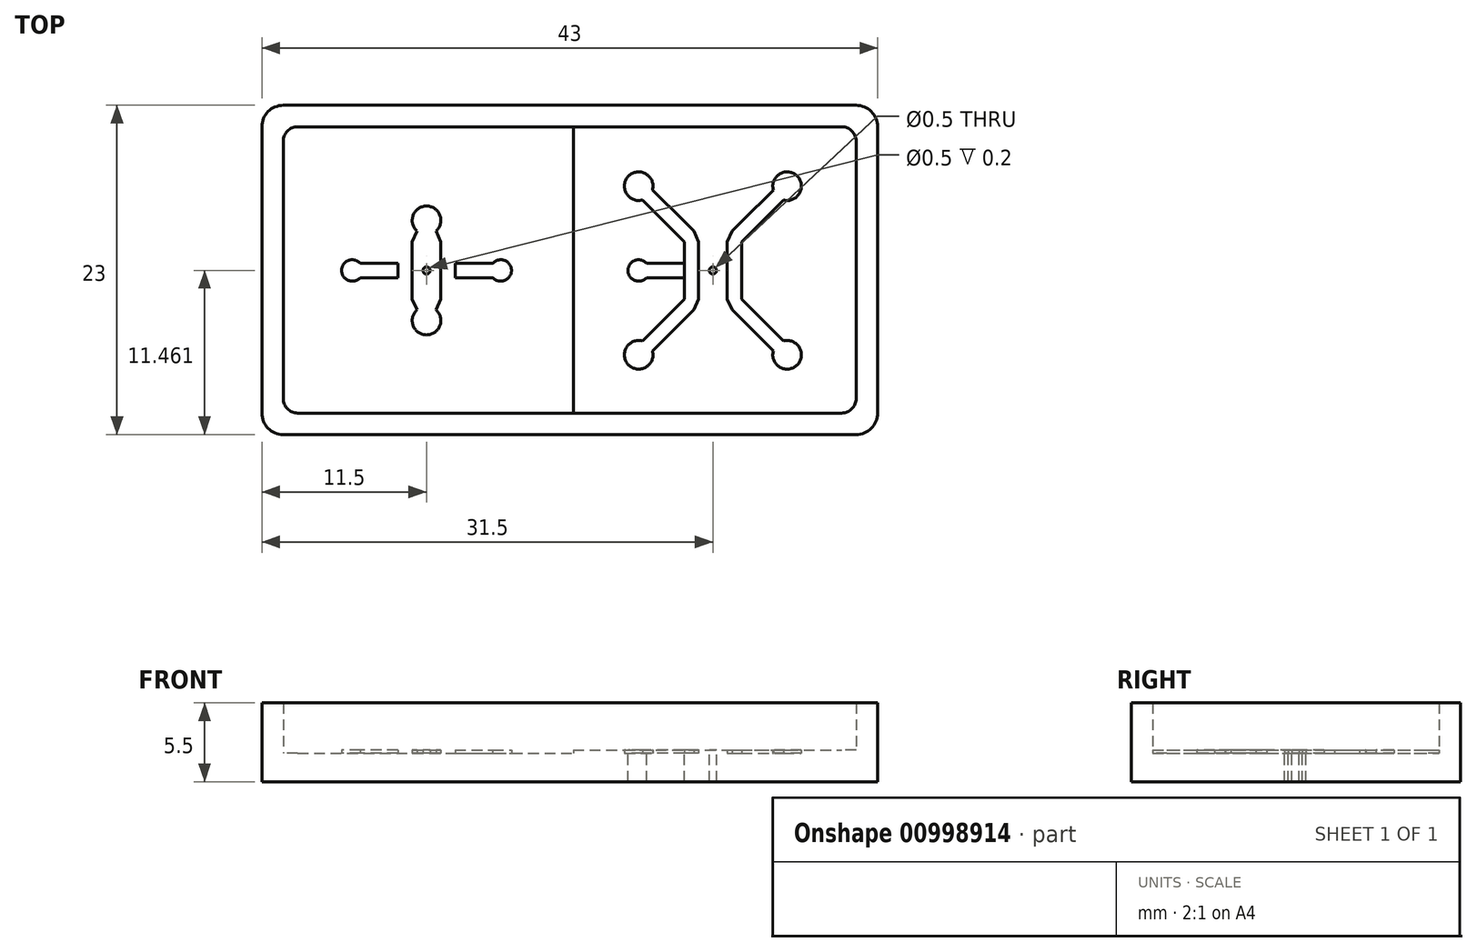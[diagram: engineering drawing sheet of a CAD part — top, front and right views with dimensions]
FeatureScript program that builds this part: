
annotation { "Feature Type Name" : "Feature", "Feature Type Description" : "" }
export const myFeature = defineFeature(function(context is Context, id is Id, definition is map)
    precondition{}
    {
        {
            var Q0;
            Q0=qCreatedBy(makeId("Top.planeOp"),FACE);
            var sketch = newSketch(context, id + "F0", { "sketchPlane" : qUnion([Q0])});
            skLineSegment(sketch, "E0.bottom", {"start": v(1, 0) * mm, "end": v(39, 0) * mm});
            skLineSegment(sketch, "E0.top", {"start": v(1, 20) * mm, "end": v(39, 20) * mm});
            skLineSegment(sketch, "E0.left", {"start": v(0, 1) * mm, "end": v(0, 19) * mm});
            skLineSegment(sketch, "E0.right", {"start": v(40, 1) * mm, "end": v(40, 19) * mm});
            skLineSegment(sketch, "E1.right", {"start": v(11, 9.96) * mm, "end": v(11, 11.96) * mm});
            skLineSegment(sketch, "E2.MirrorCS", {"start": v(9, 9.96) * mm, "end": v(9, 11.96) * mm});
            skLineSegment(sketch, "E3.MirrorCS", {"start": v(11, 9.96) * mm, "end": v(11, 7.96) * mm});
            skLineSegment(sketch, "E4.MirrorCS", {"start": v(9, 9.96) * mm, "end": v(9, 7.96) * mm});
            skLineSegment(sketch, "E5", {"start": v(10.66, 7.21) * mm, "end": v(11, 7.96) * mm});
            skLineSegment(sketch, "E6", {"start": v(9, 7.96) * mm, "end": v(9.34, 7.21) * mm});
            skCircle(sketch, "E7", {"center": v(10, 9.96) * mm, "radius": 0.25 * mm});
            skArc(sketch, "E8", {"start": v(9.34, 7.21) * mm, "mid": v(10, 5.46) * mm, "end": v(10.66, 7.21) * mm});
            skLineSegment(sketch, "E9.left", {"start": v(11, 11.96) * mm, "end": v(11, 9.96) * mm});
            skLineSegment(sketch, "E9.right", {"start": v(12, 11.96) * mm, "end": v(12, 9.96) * mm});
            skLineSegment(sketch, "E10.MirrorCS", {"start": v(12, 7.96) * mm, "end": v(12, 9.96) * mm});
            skLineSegment(sketch, "E11", {"start": v(11, 7.96) * mm, "end": v(11.34, 7.21) * mm});
            skLineSegment(sketch, "E12", {"start": v(11.34, 7.21) * mm, "end": v(12, 6.55) * mm});
            skLineSegment(sketch, "E13", {"start": v(12, 6.55) * mm, "end": v(14.22, 4.33) * mm});
            skArc(sketch, "E14", {"start": v(14.22, 4.33) * mm, "mid": v(15.89, 3.36) * mm, "end": v(14.92, 5.04) * mm});
            skArc(sketch, "E15.MirrorCS", {"start": v(9.34, 12.71) * mm, "mid": v(10, 14.46) * mm, "end": v(10.66, 12.71) * mm});
            skLineSegment(sketch, "E16.MirrorCS", {"start": v(10.66, 12.71) * mm, "end": v(11, 11.96) * mm});
            skLineSegment(sketch, "E17.MirrorCS", {"start": v(9, 11.96) * mm, "end": v(9.34, 12.71) * mm});
            skLineSegment(sketch, "E18.MirrorCS", {"start": v(11, 11.96) * mm, "end": v(11.34, 12.71) * mm});
            skLineSegment(sketch, "E19.MirrorCS", {"start": v(11.34, 12.71) * mm, "end": v(12, 13.37) * mm});
            skLineSegment(sketch, "E20.MirrorCS", {"start": v(12, 13.37) * mm, "end": v(14.22, 15.6) * mm});
            skArc(sketch, "E21.MirrorCS", {"start": v(14.22, 15.6) * mm, "mid": v(15.89, 16.56) * mm, "end": v(14.92, 14.88) * mm});
            skLineSegment(sketch, "E22", {"start": v(12, 7.96) * mm, "end": v(14.92, 5.04) * mm});
            skLineSegment(sketch, "E23.MirrorCS", {"start": v(12, 11.96) * mm, "end": v(14.92, 14.88) * mm});
            skLineSegment(sketch, "E24.MirrorCS", {"start": v(9, 11.96) * mm, "end": v(8.66, 12.71) * mm});
            skLineSegment(sketch, "E25.MirrorCS", {"start": v(9, 7.96) * mm, "end": v(8.66, 7.21) * mm});
            skLineSegment(sketch, "E26.MirrorCS", {"start": v(8.66, 12.71) * mm, "end": v(8, 13.37) * mm});
            skLineSegment(sketch, "E27.MirrorCS", {"start": v(8, 13.37) * mm, "end": v(5.78, 15.6) * mm});
            skArc(sketch, "E28.MirrorCS", {"start": v(5.78, 15.6) * mm, "mid": v(4.11, 16.56) * mm, "end": v(5.08, 14.88) * mm});
            skLineSegment(sketch, "E29.MirrorCS", {"start": v(8, 11.96) * mm, "end": v(5.08, 14.88) * mm});
            skLineSegment(sketch, "E30.MirrorCS", {"start": v(8, 11.96) * mm, "end": v(8, 9.96) * mm});
            skLineSegment(sketch, "E31.MirrorCS", {"start": v(8, 7.96) * mm, "end": v(8, 9.96) * mm});
            skArc(sketch, "E32.MirrorCS", {"start": v(5.78, 4.33) * mm, "mid": v(4.11, 3.36) * mm, "end": v(5.08, 5.04) * mm});
            skLineSegment(sketch, "E33.MirrorCS", {"start": v(8, 7.96) * mm, "end": v(5.08, 5.04) * mm});
            skLineSegment(sketch, "E34.MirrorCS", {"start": v(8, 6.55) * mm, "end": v(5.78, 4.33) * mm});
            skLineSegment(sketch, "E35.MirrorCS", {"start": v(8.66, 7.21) * mm, "end": v(8, 6.55) * mm});
            skLineSegment(sketch, "E36", {"start": v(12, 10.46) * mm, "end": v(14.62, 10.46) * mm});
            skLineSegment(sketch, "E37", {"start": v(12, 9.46) * mm, "end": v(14.62, 9.46) * mm});
            skArc(sketch, "E38", {"start": v(14.81, 10.61) * mm, "mid": v(14.71, 10.55) * mm, "end": v(14.62, 10.46) * mm});
            skArc(sketch, "E39", {"start": v(14.62, 9.46) * mm, "mid": v(15.92, 9.84) * mm, "end": v(14.81, 10.61) * mm});
            skLineSegment(sketch, "E40.MirrorCS", {"start": v(8, 10.46) * mm, "end": v(5.38, 10.46) * mm});
            skLineSegment(sketch, "E41.MirrorCS", {"start": v(8, 9.46) * mm, "end": v(5.38, 9.46) * mm});
            skArc(sketch, "E42.MirrorCS", {"start": v(5.38, 9.46) * mm, "mid": v(4.08, 9.84) * mm, "end": v(5.19, 10.61) * mm});
            skArc(sketch, "E43.MirrorCS", {"start": v(5.19, 10.61) * mm, "mid": v(5.29, 10.55) * mm, "end": v(5.38, 10.46) * mm});
            skPoint(sketch, "E44.startSnap0", {"position": v(16, 9.96) * mm});
            skPoint(sketch, "E44.startSnap1", {"position": v(15.92, 9.84) * mm});
            skPoint(sketch, "E44.endSnap0", {"position": v(15.92, 9.84) * mm});
            skLineSegment(sketch, "E45", {"start": v(-1.5, 20) * mm, "end": v(-1.5, 0) * mm});
            skLineSegment(sketch, "E46", {"start": v(0, 21.5) * mm, "end": v(40, 21.5) * mm});
            skArc(sketch, "E47", {"start": v(0, 21.5) * mm, "mid": v(-1.06, 21.06) * mm, "end": v(-1.5, 20) * mm});
            skLineSegment(sketch, "E48.MirrorCS", {"start": v(0, -1.5) * mm, "end": v(40, -1.5) * mm});
            skArc(sketch, "E49.MirrorCS", {"start": v(0, -1.5) * mm, "mid": v(-1.06, -1.06) * mm, "end": v(-1.5, 0) * mm});
            skArc(sketch, "E50.MirrorCS", {"start": v(40, 21.5) * mm, "mid": v(41.06, 21.06) * mm, "end": v(41.5, 20) * mm});
            skLineSegment(sketch, "E51.MirrorCS", {"start": v(41.5, 20) * mm, "end": v(41.5, 0) * mm});
            skArc(sketch, "E52.MirrorCS", {"start": v(40, -1.5) * mm, "mid": v(41.06, -1.06) * mm, "end": v(41.5, 0) * mm});
            skArc(sketch, "E53.filletArc", {"start": v(1, 20) * mm, "mid": v(0.3, 19.7) * mm, "end": v(0, 19) * mm});
            skArc(sketch, "E54.filletArc", {"start": v(40, 19) * mm, "mid": v(39.7, 19.7) * mm, "end": v(39, 20) * mm});
            skArc(sketch, "E55.filletArc", {"start": v(39, 0) * mm, "mid": v(39.7, 0.3) * mm, "end": v(40, 1) * mm});
            skArc(sketch, "E56.filletArc", {"start": v(0, 1) * mm, "mid": v(0.3, 0.3) * mm, "end": v(1, 0) * mm});
            skLineSegment(sketch, "E57.MirrorCS", {"start": v(31.34, 12.71) * mm, "end": v(32, 13.37) * mm});
            skLineSegment(sketch, "E58.MirrorCS", {"start": v(29, 11.96) * mm, "end": v(28.66, 12.71) * mm});
            skLineSegment(sketch, "E59.MirrorCS", {"start": v(31.34, 7.21) * mm, "end": v(32, 6.55) * mm});
            skLineSegment(sketch, "E60.MirrorCS", {"start": v(28.66, 7.21) * mm, "end": v(28, 6.55) * mm});
            skLineSegment(sketch, "E61.MirrorCS", {"start": v(31, 11.96) * mm, "end": v(31.34, 12.71) * mm});
            skLineSegment(sketch, "E62.MirrorCS", {"start": v(29.34, 7.21) * mm, "end": v(29, 7.96) * mm});
            skArc(sketch, "E63.MirrorCS", {"start": v(25.19, 10.61) * mm, "mid": v(25.29, 10.55) * mm, "end": v(25.38, 10.46) * mm});
            skLineSegment(sketch, "E64.MirrorCS", {"start": v(31, 11.96) * mm, "end": v(30.66, 12.71) * mm});
            skArc(sketch, "E65.MirrorCS", {"start": v(34.81, 10.61) * mm, "mid": v(34.71, 10.55) * mm, "end": v(34.62, 10.46) * mm});
            skLineSegment(sketch, "E66.MirrorCS", {"start": v(29.34, 12.71) * mm, "end": v(29, 11.96) * mm});
            skLineSegment(sketch, "E67.MirrorCS", {"start": v(29, 7.96) * mm, "end": v(28.66, 7.21) * mm});
            skLineSegment(sketch, "E68.MirrorCS", {"start": v(28.66, 12.71) * mm, "end": v(28, 13.37) * mm});
            skLineSegment(sketch, "E69.MirrorCS", {"start": v(31, 7.96) * mm, "end": v(30.66, 7.21) * mm});
            skLineSegment(sketch, "E70.MirrorCS", {"start": v(29, 9.96) * mm, "end": v(29, 11.96) * mm});
            skCircle(sketch, "E71.MirrorC", {"center": v(30, 9.96) * mm, "radius": 0.25 * mm});
            skLineSegment(sketch, "E72.MirrorCS", {"start": v(31, 7.96) * mm, "end": v(31.34, 7.21) * mm});
            skPoint(sketch, "E73.MirrorP", {"position": v(24.08, 9.84) * mm});
            skLineSegment(sketch, "E74.MirrorCS", {"start": v(31, 9.96) * mm, "end": v(31, 11.96) * mm});
            skLineSegment(sketch, "E75.MirrorCS", {"start": v(28, 11.96) * mm, "end": v(28, 9.96) * mm});
            skPoint(sketch, "E76.MirrorP", {"position": v(24, 9.96) * mm});
            skLineSegment(sketch, "E77.MirrorCS", {"start": v(29, 11.96) * mm, "end": v(29, 9.96) * mm});
            skLineSegment(sketch, "E78.MirrorCS", {"start": v(29, 9.96) * mm, "end": v(29, 7.96) * mm});
            skArc(sketch, "E79.MirrorCS", {"start": v(34.22, 15.6) * mm, "mid": v(35.89, 16.56) * mm, "end": v(34.92, 14.88) * mm});
            skLineSegment(sketch, "E80.MirrorCS", {"start": v(32, 11.96) * mm, "end": v(34.92, 14.88) * mm});
            skLineSegment(sketch, "E81.MirrorCS", {"start": v(28, 11.96) * mm, "end": v(25.08, 14.88) * mm});
            skLineSegment(sketch, "E82.MirrorCS", {"start": v(28, 7.96) * mm, "end": v(25.08, 5.04) * mm});
            skArc(sketch, "E83.MirrorCS", {"start": v(30.66, 7.21) * mm, "mid": v(30, 5.46) * mm, "end": v(29.34, 7.21) * mm});
            skArc(sketch, "E84.MirrorCS", {"start": v(25.78, 4.33) * mm, "mid": v(24.11, 3.36) * mm, "end": v(25.08, 5.04) * mm});
            skLineSegment(sketch, "E85.MirrorCS", {"start": v(31, 9.96) * mm, "end": v(31, 7.96) * mm});
            skLineSegment(sketch, "E86.MirrorCS", {"start": v(32, 6.55) * mm, "end": v(34.22, 4.33) * mm});
            skLineSegment(sketch, "E87.MirrorCS", {"start": v(32, 10.46) * mm, "end": v(34.62, 10.46) * mm});
            skArc(sketch, "E88.MirrorCS", {"start": v(25.78, 15.6) * mm, "mid": v(24.11, 16.56) * mm, "end": v(25.08, 14.88) * mm});
            skLineSegment(sketch, "E89.MirrorCS", {"start": v(32, 13.37) * mm, "end": v(34.22, 15.6) * mm});
            skLineSegment(sketch, "E90.MirrorCS", {"start": v(32, 11.96) * mm, "end": v(32, 9.96) * mm});
            skLineSegment(sketch, "E91.MirrorCS", {"start": v(28, 7.96) * mm, "end": v(28, 9.96) * mm});
            skLineSegment(sketch, "E92.MirrorCS", {"start": v(28, 9.46) * mm, "end": v(25.38, 9.46) * mm});
            skLineSegment(sketch, "E93.MirrorCS", {"start": v(32, 9.46) * mm, "end": v(34.62, 9.46) * mm});
            skLineSegment(sketch, "E94.MirrorCS", {"start": v(32, 7.96) * mm, "end": v(32, 9.96) * mm});
            skLineSegment(sketch, "E95.MirrorCS", {"start": v(28, 10.46) * mm, "end": v(25.38, 10.46) * mm});
            skLineSegment(sketch, "E96.MirrorCS", {"start": v(28, 6.55) * mm, "end": v(25.78, 4.33) * mm});
            skArc(sketch, "E97.MirrorCS", {"start": v(30.66, 12.71) * mm, "mid": v(30, 14.46) * mm, "end": v(29.34, 12.71) * mm});
            skArc(sketch, "E98.MirrorCS", {"start": v(34.62, 9.46) * mm, "mid": v(35.92, 9.84) * mm, "end": v(34.81, 10.61) * mm});
            skArc(sketch, "E99.MirrorCS", {"start": v(34.22, 4.33) * mm, "mid": v(35.89, 3.36) * mm, "end": v(34.92, 5.04) * mm});
            skArc(sketch, "E100.MirrorCS", {"start": v(25.38, 9.46) * mm, "mid": v(24.08, 9.84) * mm, "end": v(25.19, 10.61) * mm});
            skLineSegment(sketch, "E101.MirrorCS", {"start": v(32, 7.96) * mm, "end": v(34.92, 5.04) * mm});
            skLineSegment(sketch, "E102.MirrorCS", {"start": v(28, 13.37) * mm, "end": v(25.78, 15.6) * mm});
            skLineSegment(sketch, "E103", {"start": v(20.25, 0) * mm, "end": v(20.25, 20) * mm});
            skLineSegment(sketch, "E104.MirrorCS", {"start": v(19.75, 0) * mm, "end": v(19.75, 20) * mm});
            skPoint(sketch, "E105.newPointA", {"position": v(-3, 23) * mm});
            skLineSegment(sketch, "E106", {"start": v(19.75, 10) * mm, "end": v(17.13, 10) * mm});
            skSolve(sketch);
        }
        {
            var Q0;
            Q0=makeQuery(id+"F0.imprint","IMPRINT",FACE,{"disambiguationData":[TD([[makeQuery(id+"F0.imprint","IMPRINT",EDGE,{"derivedFrom":sQuery(id+"F0.wireOp",EDGE,"E0.left")}),1.0]])]});
            var Q1;
            Q1=makeQuery(id+"F0.imprint","IMPRINT",FACE,{"disambiguationData":[TD([[makeQuery(id+"F0.imprint","IMPRINT",EDGE,{"derivedFrom":sQuery(id+"F0.wireOp",EDGE,"E0.left")}),-1.0]])]});
            var Q2;
            Q2=makeQuery(id+"F0.imprint","IMPRINT",FACE,{"disambiguationData":[TD([[makeQuery(id+"F0.imprint","IMPRINT",EDGE,{"derivedFrom":sQuery(id+"F0.wireOp",EDGE,"E2.MirrorCS")}),-1.0]])]});
            var Q3;
            Q3=makeQuery(id+"F0.imprint","IMPRINT",FACE,{"disambiguationData":[TD([[makeQuery(id+"F0.imprint","IMPRINT",EDGE,{"derivedFrom":sQuery(id+"F0.wireOp",EDGE,"E2.MirrorCS")}),1.0]])]});
            var Q4;
            {var subQ0=sQuery(id+"F0.wireOp",EDGE,"E40.MirrorCS");Q4=makeQuery(id+"F0.imprint","IMPRINT",FACE,{"disambiguationData":[TD([[makeQuery(id+"F0.imprint","IMPRINT",EDGE,{"derivedFrom":subQ0}),1.0]])]});}
            var Q5;
            Q5=makeQuery(id+"F0.imprint","IMPRINT",FACE,{"disambiguationData":[TD([[makeQuery(id+"F0.imprint","IMPRINT",EDGE,{"derivedFrom":sQuery(id+"F0.wireOp",EDGE,"E3.MirrorCS")}),1.0]])]});
            var Q6;
            {var subQ4=sQuery(id+"F0.wireOp",EDGE,"E36");Q6=makeQuery(id+"F0.imprint","IMPRINT",FACE,{"disambiguationData":[TD([[makeQuery(id+"F0.imprint","IMPRINT",EDGE,{"derivedFrom":subQ4}),-1.0]])]});}
            var Q7;
            {var subQ4=sQuery(id+"F0.wireOp",EDGE,"E103");Q7=makeQuery(id+"F0.imprint","IMPRINT",FACE,{"disambiguationData":[TD([[makeQuery(id+"F0.imprint","IMPRINT",EDGE,{"derivedFrom":subQ4}),1.0]])]});}
            var Q8;
            Q8=makeQuery(id+"F0.imprint","IMPRINT",FACE,{"disambiguationData":[TD([[makeQuery(id+"F0.imprint","IMPRINT",EDGE,{"derivedFrom":sQuery(id+"F0.wireOp",EDGE,"E0.right")}),1.0]])]});
            var Q9;
            Q9=makeQuery(id+"F0.imprint","IMPRINT",FACE,{"disambiguationData":[TD([[makeQuery(id+"F0.imprint","IMPRINT",EDGE,{"derivedFrom":sQuery(id+"F0.wireOp",EDGE,"E65.MirrorCS")}),1.0]])]});
            var Q10;
            Q10=makeQuery(id+"F0.imprint","IMPRINT",FACE,{"disambiguationData":[TD([[makeQuery(id+"F0.imprint","IMPRINT",EDGE,{"derivedFrom":sQuery(id+"F0.wireOp",EDGE,"E57.MirrorCS")}),-1.0]])]});
            var Q11;
            Q11=makeQuery(id+"F0.imprint","IMPRINT",FACE,{"disambiguationData":[TD([[makeQuery(id+"F0.imprint","IMPRINT",EDGE,{"derivedFrom":sQuery(id+"F0.wireOp",EDGE,"E62.MirrorCS")}),-1.0]])]});
            var Q12;
            Q12=makeQuery(id+"F0.imprint","IMPRINT",FACE,{"disambiguationData":[TD([[makeQuery(id+"F0.imprint","IMPRINT",EDGE,{"derivedFrom":sQuery(id+"F0.wireOp",EDGE,"E58.MirrorCS")}),1.0]])]});
            var Q13;
            Q13=makeQuery(id+"F0.imprint","IMPRINT",FACE,{"disambiguationData":[TD([[makeQuery(id+"F0.imprint","IMPRINT",EDGE,{"derivedFrom":sQuery(id+"F0.wireOp",EDGE,"E63.MirrorCS")}),-1.0]])]});
            var Q14;
            Q14=makeQuery(id+"F0.imprint","IMPRINT",FACE,{"disambiguationData":[TD([[makeQuery(id+"F0.imprint","IMPRINT",EDGE,{"derivedFrom":sQuery(id+"F0.wireOp",EDGE,"E71.MirrorC")}),-1.0]])]});
            var Q15;
            Q15=makeQuery(id+"F0.imprint","IMPRINT",FACE,{"disambiguationData":[TD([[makeQuery(id+"F0.imprint","IMPRINT",EDGE,{"derivedFrom":sQuery(id+"F0.wireOp",EDGE,"E7")}),1.0]])]});
            extrude(context, id + "F1", {"entities" : qUnion([Q0, Q1, Q2, Q3, Q4, Q5, Q6, Q7, Q8, Q9, Q10, Q11, Q12, Q13, Q14, Q15]), "depth" : -2 * mm, "offsetDistance" : 25 * mm});
        }
        {
            var Q0;
            Q0=makeQuery(id+"F0.imprint","IMPRINT",FACE,{"disambiguationData":[TD([[makeQuery(id+"F0.imprint","IMPRINT",EDGE,{"derivedFrom":sQuery(id+"F0.wireOp",EDGE,"E0.left")}),1.0]])]});
            extrude(context, id + "F2", {"entities" : qUnion([Q0]), "operationType" : NewBodyOperationType.ADD, "depth" : 3.5 * mm, "offsetDistance" : 25 * mm});
        }
        {
            var Q0;
            Q0=makeQuery(id+"F0.imprint","IMPRINT",FACE,{"disambiguationData":[TD([[makeQuery(id+"F0.imprint","IMPRINT",EDGE,{"derivedFrom":sQuery(id+"F0.wireOp",EDGE,"E2.MirrorCS")}),-1.0]])]});
            var Q1;
            {var subQ0=sQuery(id+"F0.wireOp",EDGE,"E40.MirrorCS");Q1=makeQuery(id+"F0.imprint","IMPRINT",FACE,{"disambiguationData":[TD([[makeQuery(id+"F0.imprint","IMPRINT",EDGE,{"derivedFrom":subQ0}),1.0]])]});}
            var Q2;
            {var subQ4=sQuery(id+"F0.wireOp",EDGE,"E36");Q2=makeQuery(id+"F0.imprint","IMPRINT",FACE,{"disambiguationData":[TD([[makeQuery(id+"F0.imprint","IMPRINT",EDGE,{"derivedFrom":subQ4}),-1.0]])]});}
            var Q3;
            Q3=makeQuery(id+"F0.imprint","IMPRINT",FACE,{"disambiguationData":[TD([[makeQuery(id+"F0.imprint","IMPRINT",EDGE,{"derivedFrom":sQuery(id+"F0.wireOp",EDGE,"E63.MirrorCS")}),-1.0]])]});
            var Q4;
            Q4=makeQuery(id+"F0.imprint","IMPRINT",FACE,{"disambiguationData":[TD([[makeQuery(id+"F0.imprint","IMPRINT",EDGE,{"derivedFrom":sQuery(id+"F0.wireOp",EDGE,"E62.MirrorCS")}),-1.0]])]});
            var Q5;
            Q5=makeQuery(id+"F0.imprint","IMPRINT",FACE,{"disambiguationData":[TD([[makeQuery(id+"F0.imprint","IMPRINT",EDGE,{"derivedFrom":sQuery(id+"F0.wireOp",EDGE,"E65.MirrorCS")}),1.0]])]});
            extrude(context, id + "F3", {"entities" : qUnion([Q0, Q1, Q2, Q3, Q4, Q5]), "operationType" : NewBodyOperationType.ADD, "depth" : .2 * mm, "offsetDistance" : 25 * mm});
        }
    });
